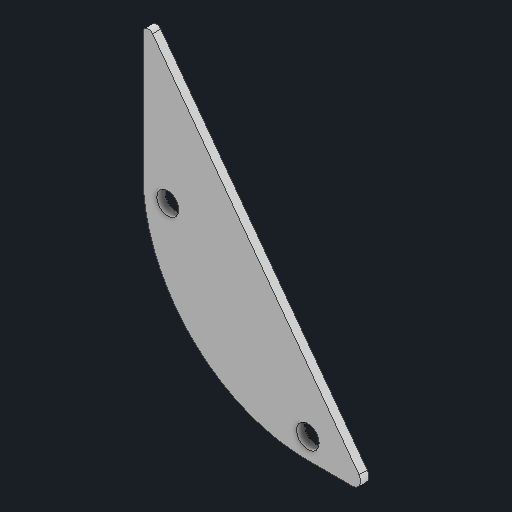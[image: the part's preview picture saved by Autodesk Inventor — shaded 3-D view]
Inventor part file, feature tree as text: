
AUTODESK INVENTOR PART (.ipt)
format: ipt  version: 2025 (Build 290162000, 162)  size: 96,768 bytes
history: native  units: in
note: dims shown in document units (in); Inventor stores cm internally (conversion verified against a paired STEP export)
features: extrude x1, sketch x1
ambient origin geometry x8: Origin, YZ Plane, XZ Plane, XY Plane, X Axis, Y Axis, Z Axis, Center Point
bodies: Solid1 (feature_tree)
feature tree (2):
  extrude  "Extrusion1"  Depth=0.0625in TaperAngle=0.0deg
  sketch  "Sketch1"  dims[d0=0.04in d1=0.0625in d2=1.25in d3=0.0625in d4=0.0in]
